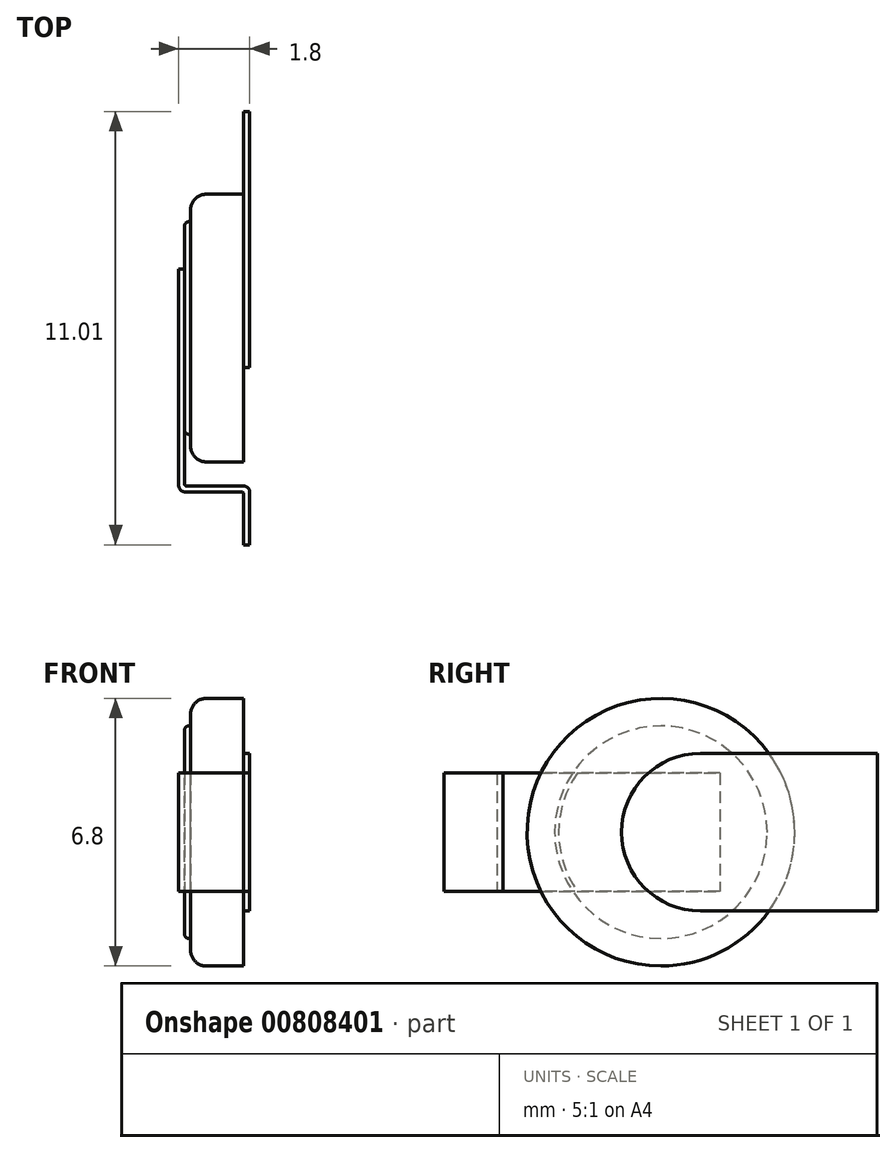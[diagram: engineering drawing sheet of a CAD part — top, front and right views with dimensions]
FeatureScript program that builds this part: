
annotation { "Feature Type Name" : "Feature", "Feature Type Description" : "" }
export const myFeature = defineFeature(function(context is Context, id is Id, definition is map)
    precondition{}
    {
        {
            var Q0;
            Q0=qCreatedBy(makeId("Top.planeOp"),FACE);
            var sketch = newSketch(context, id + "F0", { "sketchPlane" : qUnion([Q0])});
            skLineSegment(sketch, "E0", {"start": v(0, 1.5) * mm, "end": v(0, 0) * mm});
            skLineSegment(sketch, "E1", {"start": v(0, 0) * mm, "end": v(0, -4) * mm});
            skLineSegment(sketch, "E2", {"start": v(0.17, -4.17) * mm, "end": v(1.6, -4.17) * mm});
            skLineSegment(sketch, "E3", {"start": v(1.65, -4.21) * mm, "end": v(1.65, -5.51) * mm});
            skLineSegment(sketch, "E4", {"start": v(1.65, -5.51) * mm, "end": v(1.8, -5.51) * mm});
            skLineSegment(sketch, "E5", {"start": v(1.8, -5.51) * mm, "end": v(1.8, -4.17) * mm});
            skLineSegment(sketch, "E6", {"start": v(1.65, -4.02) * mm, "end": v(0.2, -4.02) * mm});
            skLineSegment(sketch, "E7", {"start": v(0.15, -3.97) * mm, "end": v(0.15, 1.5) * mm});
            skLineSegment(sketch, "E8", {"start": v(0.15, 1.5) * mm, "end": v(0, 1.5) * mm});
            skPoint(sketch, "E9.visualSharp", {"position": v(0, -4.17) * mm});
            skArc(sketch, "E9.filletArc", {"start": v(0, -4) * mm, "mid": v(0.05, -4.12) * mm, "end": v(0.17, -4.17) * mm});
            skPoint(sketch, "E10.visualSharp", {"position": v(0.15, -4.02) * mm});
            skArc(sketch, "E11.filletArc", {"start": v(0.15, -3.97) * mm, "mid": v(0.16, -4) * mm, "end": v(0.2, -4.02) * mm});
            skPoint(sketch, "E12.visualSharp", {"position": v(1.65, -4.17) * mm});
            skArc(sketch, "E12.filletArc", {"start": v(1.65, -4.21) * mm, "mid": v(1.64, -4.18) * mm, "end": v(1.6, -4.17) * mm});
            skPoint(sketch, "E13.visualSharp", {"position": v(1.8, -4.02) * mm});
            skArc(sketch, "E13.filletArc", {"start": v(1.8, -4.17) * mm, "mid": v(1.76, -4.06) * mm, "end": v(1.65, -4.02) * mm});
            skLineSegment(sketch, "E14.bottom", {"start": v(0.3, 2.7) * mm, "end": v(0.25, 2.7) * mm});
            skLineSegment(sketch, "E14.top", {"start": v(0.3, 0) * mm, "end": v(0.15, 0) * mm});
            skLineSegment(sketch, "E14.left", {"start": v(0.3, 2.7) * mm, "end": v(0.3, 0) * mm});
            skLineSegment(sketch, "E14.right", {"start": v(0.15, 2.6) * mm, "end": v(0.15, 0) * mm});
            skPoint(sketch, "E15.visualSharp", {"position": v(0.15, 2.7) * mm});
            skArc(sketch, "E15.filletArc", {"start": v(0.25, 2.7) * mm, "mid": v(0.18, 2.67) * mm, "end": v(0.15, 2.6) * mm});
            skPoint(sketch, "E16.visualSharp", {"position": v(0.15, 0) * mm});
            skLineSegment(sketch, "E16.filletArc", {"start": v(0.15, 0) * mm, "end": v(0.15, 0) * mm});
            skLineSegment(sketch, "E17", {"start": v(0.3, 1.35) * mm, "end": v(0.15, 1.3) * mm, "construction": true});
            skLineSegment(sketch, "E18.bottom", {"start": v(1.65, 3.4) * mm, "end": v(0.7, 3.4) * mm});
            skLineSegment(sketch, "E18.top", {"start": v(1.65, 0) * mm, "end": v(0.3, 0) * mm});
            skLineSegment(sketch, "E18.left", {"start": v(1.65, 3.4) * mm, "end": v(1.65, 0) * mm});
            skLineSegment(sketch, "E18.right", {"start": v(0.3, 3) * mm, "end": v(0.3, 0) * mm});
            skPoint(sketch, "E19.visualSharp", {"position": v(0.3, 3.4) * mm});
            skArc(sketch, "E19.filletArc", {"start": v(0.7, 3.4) * mm, "mid": v(0.42, 3.28) * mm, "end": v(0.3, 3) * mm});
            skLineSegment(sketch, "E20.bottom", {"start": v(1.8, 5.5) * mm, "end": v(1.65, 5.5) * mm});
            skLineSegment(sketch, "E20.top", {"start": v(1.8, -1) * mm, "end": v(1.65, -1) * mm});
            skLineSegment(sketch, "E20.left", {"start": v(1.8, 5.5) * mm, "end": v(1.8, -1) * mm});
            skLineSegment(sketch, "E20.right", {"start": v(1.65, 5.5) * mm, "end": v(1.65, -1) * mm});
            skSolve(sketch);
        }
        {
            var Q0;
            Q0=makeQuery(id+"F0.imprint","IMPRINT",FACE,{"disambiguationData":[TD([[makeQuery(id+"F0.imprint","IMPRINT",EDGE,{"derivedFrom":sQuery(id+"F0.wireOp",EDGE,"E0")}),1.0]])]});
            extrude(context, id + "F1", {"entities" : qUnion([Q0]), "depth" : 1.5 * mm, "offsetDistance" : 25 * mm, "hasSecondDirection" : true, "secondDirectionOppositeDirection" : true, "secondDirectionDepth" : 1.5 * mm});
        }
        {
            var Q0;
            Q0=makeQuery(id+"F0.imprint","IMPRINT",FACE,{"disambiguationData":[TD([[makeQuery(id+"F0.imprint","IMPRINT",EDGE,{"derivedFrom":sQuery(id+"F0.wireOp",EDGE,"E14.bottom")}),1.0]])]});
            var Q1;
            Q1=sQuery(id+"F0.wireOp",EDGE,"E14.top");
            revolve(context, id + "F2", {"operationType" : NewBodyOperationType.ADD, "surfaceOperationType" : NewSurfaceOperationType.NEW, "entities" : qUnion([Q0]), "axis" : qUnion([Q1]), "revolveType" : RevolveType.FULL});
        }
        {
            var Q0;
            Q0=makeQuery(id+"F0.imprint","IMPRINT",FACE,{"disambiguationData":[TD([[makeQuery(id+"F0.imprint","IMPRINT",EDGE,{"derivedFrom":sQuery(id+"F0.wireOp",EDGE,"E18.bottom")}),1.0]])]});
            var Q1;
            Q1=sQuery(id+"F0.wireOp",EDGE,"E18.top");
            revolve(context, id + "F3", {"operationType" : NewBodyOperationType.ADD, "surfaceOperationType" : NewSurfaceOperationType.NEW, "entities" : qUnion([Q0]), "axis" : qUnion([Q1]), "revolveType" : RevolveType.FULL});
        }
        {
            var Q0;
            {var subQ2=sQuery(id+"F0.wireOp",EDGE,"E20.bottom");Q0=makeQuery(id+"F0.imprint","IMPRINT",FACE,{"disambiguationData":[TD([[makeQuery(id+"F0.imprint","IMPRINT",EDGE,{"derivedFrom":subQ2}),1.0]])]});}
            extrude(context, id + "F4", {"entities" : qUnion([Q0]), "operationType" : NewBodyOperationType.ADD, "depth" : 2 * mm, "offsetDistance" : 25 * mm, "hasSecondDirection" : true, "secondDirectionOppositeDirection" : true, "secondDirectionDepth" : 2 * mm});
        }
        {
            var Q0;
            Q0=makeQuery(id+"F4.opExtrude","CAP_EDGE",EDGE,{"disambiguationData":[OSD([sQuery(id+"F0.wireOp",EDGE,"E20.top")])],"isStart":true});
            var Q1;
            Q1=makeQuery(id+"F4.opExtrude","CAP_EDGE",EDGE,{"disambiguationData":[OSD([sQuery(id+"F0.wireOp",EDGE,"E20.top")])],"isStart":false});
            fillet(context, id + "F5", {"entities" : qUnion([Q0, Q1]), "radius" : 2 * mm, "tangentPropagation" : true, "allowEdgeOverflow" : false});
        }
    });
